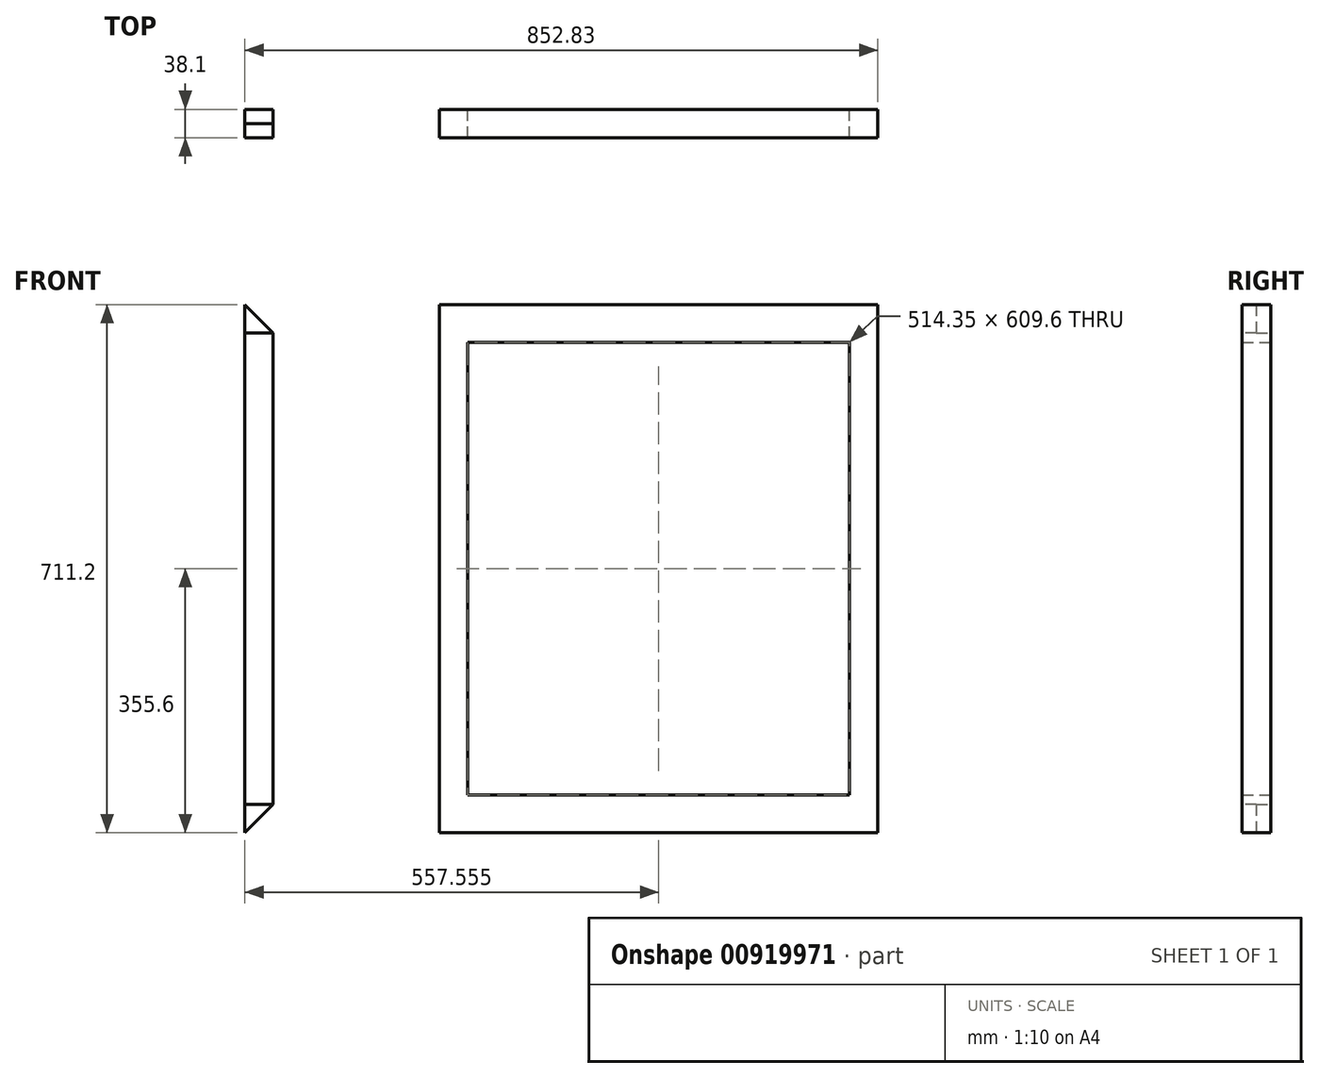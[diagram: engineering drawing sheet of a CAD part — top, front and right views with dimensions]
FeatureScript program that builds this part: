
annotation { "Feature Type Name" : "Feature", "Feature Type Description" : "" }
export const myFeature = defineFeature(function(context is Context, id is Id, definition is map)
    precondition{}
    {
        {
            var Q0;
            Q0=qCreatedBy(makeId("Front.planeOp"),FACE);
            var sketch = newSketch(context, id + "F0", { "sketchPlane" : qUnion([Q0])});
            skLineSegment(sketch, "E0", {"start": v(0, 0) * mm, "end": v(0, -711.2) * mm});
            skLineSegment(sketch, "E1", {"start": v(0, -711.2) * mm, "end": v(590.55, -711.2) * mm});
            skLineSegment(sketch, "E2", {"start": v(590.55, -711.2) * mm, "end": v(590.55, 0) * mm});
            skLineSegment(sketch, "E3", {"start": v(0, 0) * mm, "end": v(590.55, 0) * mm});
            skLineSegment(sketch, "E4.bottom", {"start": v(38.1, -50.8) * mm, "end": v(552.45, -50.8) * mm});
            skLineSegment(sketch, "E4.top", {"start": v(38.1, -660.4) * mm, "end": v(552.45, -660.4) * mm});
            skLineSegment(sketch, "E4.left", {"start": v(38.1, -50.8) * mm, "end": v(38.1, -660.4) * mm});
            skLineSegment(sketch, "E4.right", {"start": v(552.45, -50.8) * mm, "end": v(552.45, -660.4) * mm});
            skSolve(sketch);
        }
        {
            var Q0;
            Q0=makeQuery(id+"F0.imprint","IMPRINT",FACE,{"disambiguationData":[TD([[makeQuery(id+"F0.imprint","IMPRINT",EDGE,{"derivedFrom":sQuery(id+"F0.wireOp",EDGE,"E0")}),1.0]])]});
            extrude(context, id + "F1", {"entities" : qUnion([Q0]), "depth" : 38.1 * mm, "offsetDistance" : 25.4 * mm});
        }
        {
            var Q0;
            Q0=qCreatedBy(makeId("Front.planeOp"),FACE);
            var sketch = newSketch(context, id + "F2", { "sketchPlane" : qUnion([Q0])});
            skLineSegment(sketch, "E5.left", {"start": v(-262.28, 0) * mm, "end": v(-262.28, -711.2) * mm});
            skLineSegment(sketch, "E5.right", {"start": v(-224.18, -38.1) * mm, "end": v(-224.18, -673.1) * mm});
            skLineSegment(sketch, "E6", {"start": v(-262.28, 0) * mm, "end": v(-224.18, -38.1) * mm});
            skLineSegment(sketch, "E7", {"start": v(-262.28, -711.2) * mm, "end": v(-224.18, -673.1) * mm});
            skSolve(sketch);
        }
        {
            var Q0;
            Q0=makeQuery(id+"F2.imprint","IMPRINT",FACE,{"disambiguationData":[TD([[makeQuery(id+"F2.imprint","IMPRINT",EDGE,{"derivedFrom":sQuery(id+"F2.wireOp",EDGE,"E5.left")}),1.0]])]});
            extrude(context, id + "F3", {"entities" : qUnion([Q0]), "depth" : 38.1 * mm, "offsetDistance" : 25.4 * mm});
        }
        {
            var Q0;
            Q0=makeQuery(id+"F3.opExtrude","CAP_FACE",FACE,{"disambiguationData":[OSD([sQuery(id+"F2.wireOp",EDGE,"E5.left"),sQuery(id+"F2.wireOp",EDGE,"E5.right"),sQuery(id+"F2.wireOp",EDGE,"E6"),sQuery(id+"F2.wireOp",EDGE,"E7")])],"isStart":false});
            var sketch = newSketch(context, id + "F4", { "sketchPlane" : qUnion([Q0])});
            skLineSegment(sketch, "E8", {"start": v(-262.28, 0) * mm, "end": v(-224.18, -38.1) * mm});
            skLineSegment(sketch, "E9", {"start": v(-224.18, -38.1) * mm, "end": v(-262.28, -38.1) * mm});
            skLineSegment(sketch, "E10", {"start": v(-262.28, -38.1) * mm, "end": v(-262.28, 0) * mm});
            skLineSegment(sketch, "E11", {"start": v(-262.28, -711.2) * mm, "end": v(-224.18, -673.1) * mm});
            skLineSegment(sketch, "E12", {"start": v(-224.18, -673.1) * mm, "end": v(-262.28, -673.1) * mm});
            skLineSegment(sketch, "E13", {"start": v(-262.28, -673.1) * mm, "end": v(-262.28, -711.2) * mm});
            skSolve(sketch);
        }
        {
            var Q0;
            Q0=makeQuery(id+"F4.imprint","IMPRINT",FACE,{"disambiguationData":[TD([[makeQuery(id+"F4.imprint","IMPRINT",EDGE,{"derivedFrom":sQuery(id+"F4.wireOp",EDGE,"E11")}),1.0]])]});
            var Q1;
            Q1=makeQuery(id+"F4.imprint","IMPRINT",FACE,{"disambiguationData":[TD([[makeQuery(id+"F4.imprint","IMPRINT",EDGE,{"derivedFrom":sQuery(id+"F4.wireOp",EDGE,"E8")}),-1.0]])]});
            extrude(context, id + "F5", {"entities" : qUnion([Q0, Q1]), "operationType" : NewBodyOperationType.REMOVE, "oppositeDirection" : true, "depth" : 19.05 * mm, "offsetDistance" : 25.4 * mm});
        }
    });
